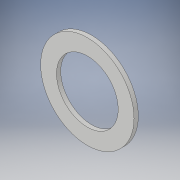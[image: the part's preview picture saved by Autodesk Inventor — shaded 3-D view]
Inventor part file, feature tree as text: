
AUTODESK INVENTOR PART (.ipt)
format: ipt  version: 2018 (Build 220112000, 112)  size: 760,320 bytes
history: native  units: mm
features: extrude x2, sketch x2
ambient origin geometry x8: Origin, YZ Plane, XZ Plane, XY Plane, X Axis, Y Axis, Z Axis, Center Point
bodies: Volumenkörper1 (feature_tree)
feature tree (4):
  extrude  "Extrusion1"  Depth=88.0mm
  extrude  "Extrusion2"  Depth=1.0mm TaperAngle=0.0deg
  sketch  "Skizze1"  dims[d0=58.2mm d1=88.0mm]
  sketch  "Skizze2"  dims[d2=4.0mm d3=0.0mm d4=1.0mm d5=0.0mm]
